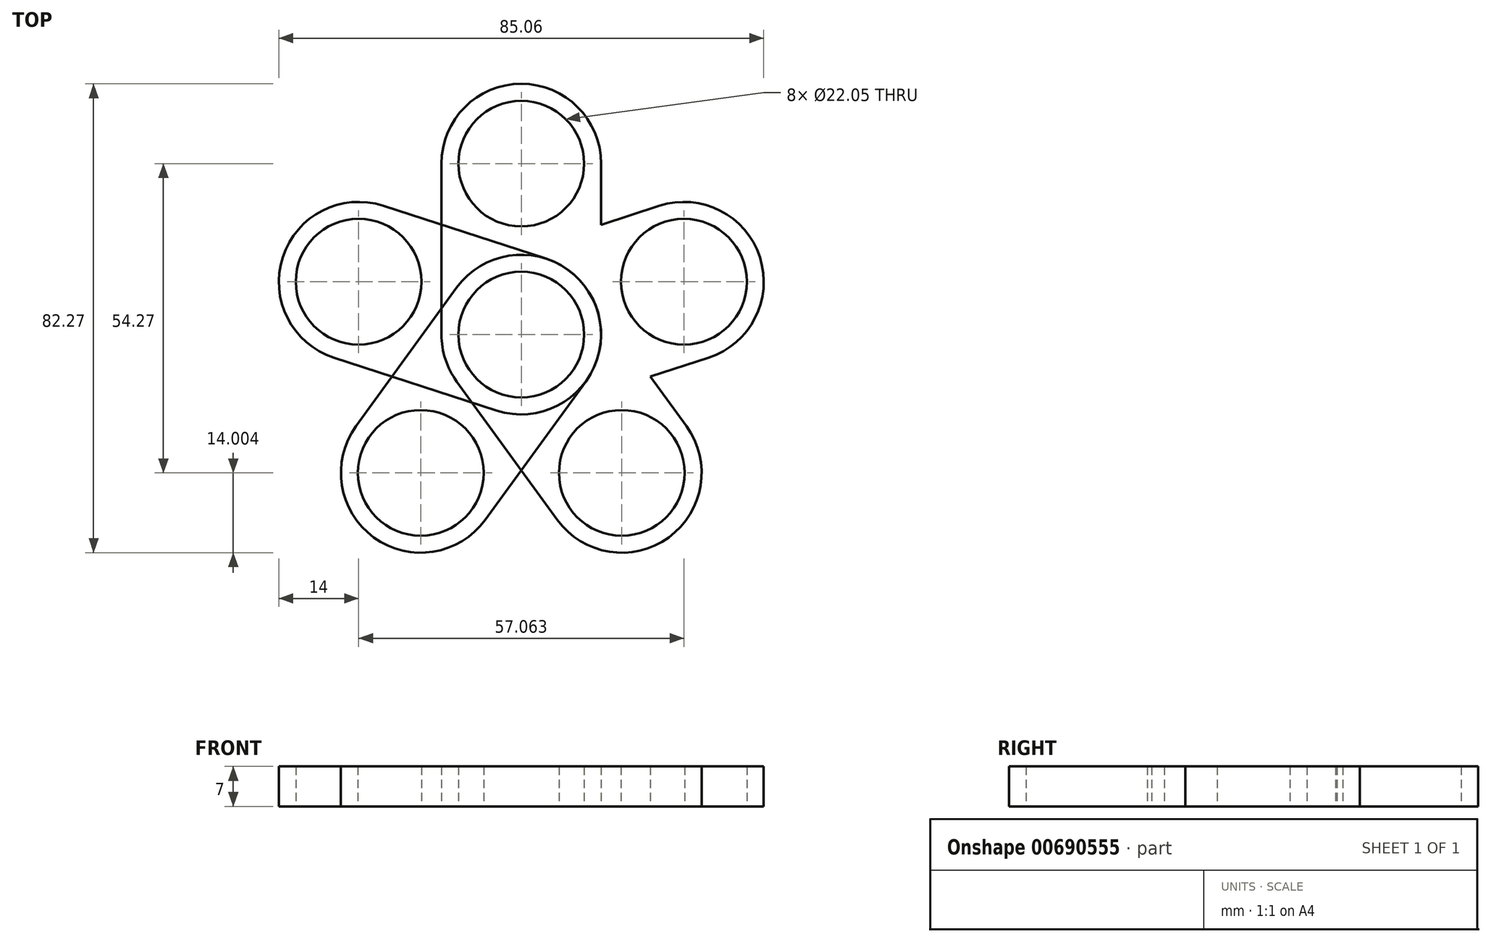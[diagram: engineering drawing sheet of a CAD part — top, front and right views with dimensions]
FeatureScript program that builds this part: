
annotation { "Feature Type Name" : "Feature", "Feature Type Description" : "" }
export const myFeature = defineFeature(function(context is Context, id is Id, definition is map)
    precondition{}
    {
        {
            var Q0;
            Q0=qCreatedBy(makeId("Top.planeOp"),FACE);
            var sketch = newSketch(context, id + "F0", { "sketchPlane" : qUnion([Q0])});
            skLineSegment(sketch, "E0.bottom", {"start": v(-5.05, 7.33) * mm, "end": v(22.95, 7.33) * mm});
            skLineSegment(sketch, "E0.top", {"start": v(-5.05, -22.67) * mm, "end": v(22.95, -22.67) * mm});
            skLineSegment(sketch, "E0.left", {"start": v(-5.05, 7.33) * mm, "end": v(-5.05, -22.67) * mm});
            skLineSegment(sketch, "E0.right", {"start": v(22.95, 7.33) * mm, "end": v(22.95, -22.67) * mm});
            skCircle(sketch, "E1", {"center": v(8.95, 7.33) * mm, "radius": 14 * mm});
            skCircle(sketch, "E2", {"center": v(8.95, 7.33) * mm, "radius": 11.03 * mm});
            skCircle(sketch, "E3", {"center": v(8.95, -22.67) * mm, "radius": 14 * mm});
            skCircle(sketch, "E4", {"center": v(8.95, -22.67) * mm, "radius": 11.03 * mm});
            skSolve(sketch);
        }
        {
            var Q0;
            Q0=qSketchRegion(id+"F0",true);
            extrude(context, id + "F1", {"entities" : qUnion([Q0]), "depth" : 7 * mm, "offsetDistance" : 25.4 * mm});
        }
        {
            var Q0;
            Q0=makeQuery(id+"F1.opExtrude","SWEPT_BODY",BODY,{"disambiguationData":[OSD([sQuery(id+"F0.wireOp",EDGE,"E0.left"),sQuery(id+"F0.wireOp",EDGE,"E0.right"),sQuery(id+"F0.wireOp",EDGE,"E1"),sQuery(id+"F0.wireOp",EDGE,"E2"),sQuery(id+"F0.wireOp",EDGE,"E3"),sQuery(id+"F0.wireOp",EDGE,"E4")])]});
            var Q1;
            Q1=makeQuery(id+"F1.opExtrude","SWEPT_FACE",FACE,{"disambiguationData":[OSD([sQuery(id+"F0.wireOp",EDGE,"E3")])]});
            circularPattern(context, id + "F2", {"entities" : qUnion([Q0]), "axis" : qUnion([Q1]), "angle" : 360 * degree, "instanceCount" : 5, "equalSpace" : true, "fullFeaturePattern" : false});
        }
        {
            var Q0;
            Q0=makeQuery(id+"F1.opExtrude","SWEPT_BODY",BODY,{"disambiguationData":[OSD([sQuery(id+"F0.wireOp",EDGE,"E0.left"),sQuery(id+"F0.wireOp",EDGE,"E0.right"),sQuery(id+"F0.wireOp",EDGE,"E1"),sQuery(id+"F0.wireOp",EDGE,"E2"),sQuery(id+"F0.wireOp",EDGE,"E3"),sQuery(id+"F0.wireOp",EDGE,"E4")])]});
            var Q1;
            Q1=makeQuery(id+"F2.opPattern","COPY",BODY,{"derivedFrom":makeQuery(id+"F1.opExtrude","SWEPT_BODY",BODY,{"disambiguationData":[OSD([sQuery(id+"F0.wireOp",EDGE,"E0.left"),sQuery(id+"F0.wireOp",EDGE,"E0.right"),sQuery(id+"F0.wireOp",EDGE,"E1"),sQuery(id+"F0.wireOp",EDGE,"E2"),sQuery(id+"F0.wireOp",EDGE,"E3"),sQuery(id+"F0.wireOp",EDGE,"E4")])]}),"instanceName":"1"});
            var Q2;
            Q2=makeQuery(id+"F2.opPattern","COPY",BODY,{"derivedFrom":makeQuery(id+"F1.opExtrude","SWEPT_BODY",BODY,{"disambiguationData":[OSD([sQuery(id+"F0.wireOp",EDGE,"E0.left"),sQuery(id+"F0.wireOp",EDGE,"E0.right"),sQuery(id+"F0.wireOp",EDGE,"E1"),sQuery(id+"F0.wireOp",EDGE,"E2"),sQuery(id+"F0.wireOp",EDGE,"E3"),sQuery(id+"F0.wireOp",EDGE,"E4")])]}),"instanceName":"2"});
            booleanBodies(context, id + "F3", {"operationType" : BooleanOperationType.UNION, "tools" : qUnion([Q0, Q1, Q2])});
        }
    });
